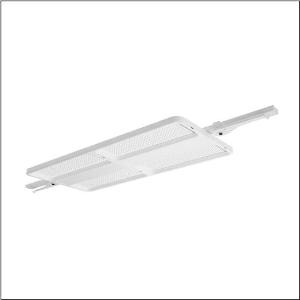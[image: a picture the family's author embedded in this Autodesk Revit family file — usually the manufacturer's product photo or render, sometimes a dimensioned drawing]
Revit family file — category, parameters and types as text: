
# Revit family: highbay_21_fur_modario_r__tragschiene_maxi_52hn11db6qma_37e2
name_source: partatom
category: Lighting Fixtures
units: mm (PartAtom-declared; Revit-internal decimal feet)

## family parameters
Cut with Voids When Loaded = No
Host = Face
Light Source = No
Part Type = Normal
Room Calculation Point = No
Round Connector Dimension = Use Diameter
Shared = No

## types (1)
- --- (1 x LED, 5650 lm, 31.4 W, 6500K)
    Apparent Load = 31 VA
    CIE Flux Codes = 89 97 99 100 100
    Color Rendering = 80
    Color Temperature = 6500K
    Default Elevation = 1800 mm
    Description = high bay luminaire Highbay 21 for Modario® trunking rail maxi; direct symmetric narrow distribution, light control with lens of PMMA; UGR ≤ 22 (X = 4H | Y = 8H | S = 0.25H | reflection values 70/50/20); luminous flux: 36.840lm; light colour: 865, colour temperature: 6500K, MacAdam ≤ 3 SDCM (initial), colour rendering: CRI > 80; luminous efficacy: 186,3lm/W; rated service life: 75.000h (L80) at AT= ta max; control: DALI 2; luminaire connection: plug, 5-pole, with phase selectionmains connection: 230..240V, AC 50/60Hz; connected load: 197,7W; protection rating (complete): IP64; insulation class (complete): insulation class I (protective earthing); protection symbol: D; impact resistance: IK06; certification: CE, UKCA; internal wiring halogen-free; luminaire LABS conformity tested according to VDMA 24364:2018-05; Suitable for use in the food industry according to the specifications of IFS-Food, HACCP and/or BRC; housing frame of high-performance plastic PA6, matt traffic white (RAL 9016); cover of PMMA; fixing on rail side of steel, galvanised, white; blank cover of PC, traffic white (RAL 9016); dimension (LxWxH): 1.496 x 442 x 72mm; permissible operating ambient temperature: -35..+50°C (reducing of maximum allowable ambient temperature of 5°C with ceiling mounting); packaging unit: 1 piece
    Height = 72 mm  [stored 0.23622 ft]
    Lamp = 1 x LED
    Lamp Light Flux = 5650 lm
    Lamp Power = 31.4 W
    Lamp count = 1
    Length = 946 mm
    Luminous efficacy = 180 lm/W
    Manufacturer = Siteco
    ModVariant = No
    Model = 52HN11DB6QMA
    Mounting Place = Ceiling
    Mounting Type = Pendant
    Number of Poles = 1
    OnlyDefault = Yes
    Power Factor = 1
    Product Name = Highbay 21 für Modario® Tragschiene maxi
    Product group = high bay luminaire
    ProductGroupID = 902
    Protection Class = Protection class I
    Protection Degree = IP 64
    RLX_Detail_Level = 1
    RLX_Emergency_Light_Flux = 0 lm
    RLX_Emergency_Type = 0
    RLX_Emergency_Type_DB = No
    RlxData = <blob elided: 127605 chars, md5=a0da535f>
    Socket = socket
    Standby Power = 0 W
    System Light Flux = 5650 lm
    System Power = 31 W
    Type Comments = : DC mode (central or group accumulator) initial emergency light level
    Type Image = l_1363248.jpg
    URL = http://relux.com
    VarID = @adj_001171
    Voltage = 0 V
    Weight = 0.00 kg
    Width = 442 mm

note: [stored X ft] marks values corroborated as IEEE doubles in the binary element streams (Revit-internal decimal feet)

## geometry (parser evidence)
native form markers: Blend x4, Sweep x10
no freeform markers — native parametric forms only
